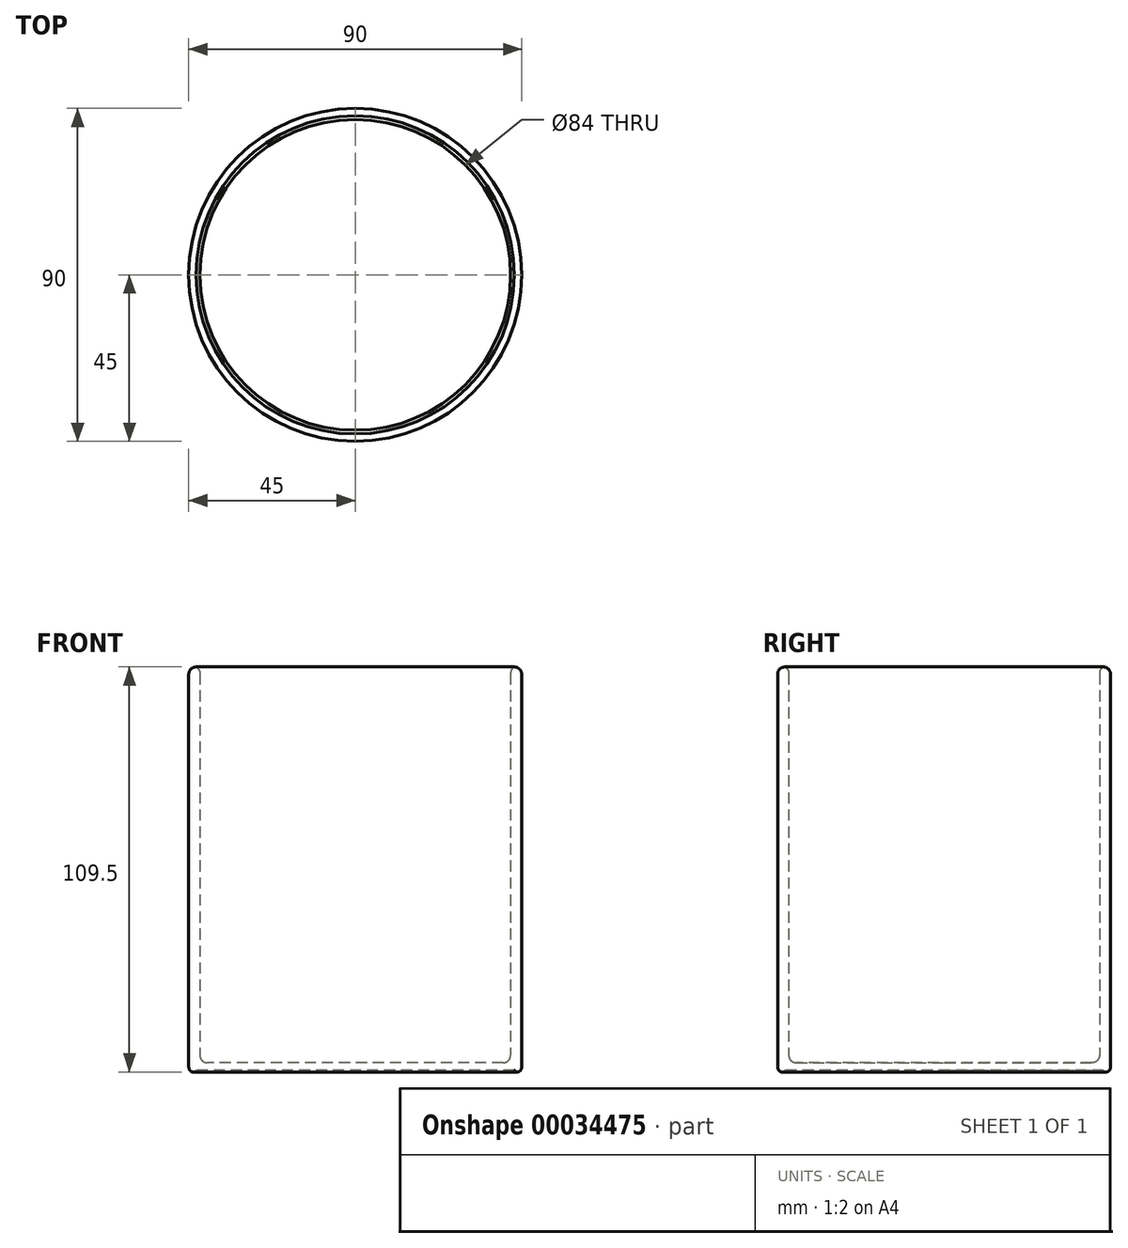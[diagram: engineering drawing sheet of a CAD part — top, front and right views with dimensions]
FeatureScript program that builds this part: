
annotation { "Feature Type Name" : "Feature", "Feature Type Description" : "" }
export const myFeature = defineFeature(function(context is Context, id is Id, definition is map)
    precondition{}
    {
        {
            var Q0;
            Q0=qCreatedBy(makeId("Top.planeOp"),FACE);
            var sketch = newSketch(context, id + "F0", { "sketchPlane" : qUnion([Q0])});
            skCircle(sketch, "E0", {"center": v(0, 0) * mm, "radius": 45 * mm});
            skSolve(sketch);
        }
        {
            var Q0;
            Q0=makeQuery(id+"F0.imprint","IMPRINT",FACE,{"disambiguationData":[TD([[makeQuery(id+"F0.imprint","IMPRINT",EDGE,{"derivedFrom":sQuery(id+"F0.wireOp",EDGE,"E0")}),1.0]])]});
            extrude(context, id + "F1", {"entities" : qUnion([Q0]), "depth" : 110 * mm});
        }
        {
            var Q0;
            Q0=makeQuery(id+"F1.opExtrude","CAP_FACE",FACE,{"disambiguationData":[OSD([sQuery(id+"F0.wireOp",EDGE,"E0")])],"isStart":false});
            shell(context, id + "F2", {"entities" : qUnion([Q0]), "thickness" : 3 * mm});
        }
        {
            var Q0;
            {var subQ0=sQuery(id+"F0.wireOp",EDGE,"E0");Q0=makeQuery(id+"F2.opShell","OFFSET_EDGE",EDGE,{"disambiguationData":[OSD([subQ0]),TDD([makeQuery(id+"F1.opExtrude","CAP_EDGE",EDGE,{"disambiguationData":[OSD([subQ0])],"isStart":true})])]});}
            fillet(context, id + "F3", {"entities" : qUnion([Q0]), "radius" : 2 * mm, "tangentPropagation" : true, "allowEdgeOverflow" : false});
        }
        {
            var Q0;
            Q0=makeQuery(id+"F1.opExtrude","CAP_EDGE",EDGE,{"disambiguationData":[OSD([sQuery(id+"F0.wireOp",EDGE,"E0")])],"isStart":true});
            fillet(context, id + "F4", {"entities" : qUnion([Q0]), "radius" : 2 * mm, "tangentPropagation" : true, "allowEdgeOverflow" : false});
        }
        {
            var Q0;
            Q0=makeQuery(id+"F1.opExtrude","CAP_EDGE",EDGE,{"disambiguationData":[OSD([sQuery(id+"F0.wireOp",EDGE,"E0")])],"isStart":false});
            fillet(context, id + "F5", {"entities" : qUnion([Q0]), "radius" : 2 * mm, "tangentPropagation" : true, "allowEdgeOverflow" : false});
        }
        {
            var Q0;
            {var subQ0=sQuery(id+"F0.wireOp",EDGE,"E0");Q0=makeQuery(id+"F2.opShell","OFFSET_EDGE",EDGE,{"disambiguationData":[OSD([subQ0]),TDD([makeQuery(id+"F1.opExtrude","CAP_EDGE",EDGE,{"disambiguationData":[OSD([subQ0])],"isStart":false})])]});}
            fillet(context, id + "F6", {"entities" : qUnion([Q0]), "radius" : 2 * mm, "tangentPropagation" : true, "allowEdgeOverflow" : false});
        }
        {
            var Q0;
            Q0=makeQuery(id+"F1.opExtrude","CAP_FACE",FACE,{"disambiguationData":[OSD([sQuery(id+"F0.wireOp",EDGE,"E0")])],"isStart":true});
            extrude(context, id + "F7", {"entities" : qUnion([Q0]), "operationType" : NewBodyOperationType.REMOVE, "oppositeDirection" : true, "depth" : 1 * mm});
        }
        {
            var Q0;
            {var subQ0=sQuery(id+"F0.wireOp",EDGE,"E0");Q0=makeQuery(id+"F7.boolean.opBoolean","MERGE",EDGE,{"derivedFrom":[makeQuery(id+"F4.opFillet","BLEND_EDGE",EDGE,{"blendedFrom":[makeQuery(id+"F1.opExtrude","CAP_EDGE",EDGE,{"disambiguationData":[OSD([subQ0])],"isStart":true}),makeQuery(id+"F1.opExtrude","CAP_FACE",FACE,{"disambiguationData":[OSD([subQ0])],"isStart":true})],"blendedInto":[makeQuery(id+"F1.opExtrude","CAP_FACE",FACE,{"disambiguationData":[OSD([subQ0])],"isStart":true})]}),makeQuery(id+"F7.opExtrude","CAP_EDGE",EDGE,{"disambiguationData":[OSD([subQ0])],"isStart":true})]});}
            fillet(context, id + "F8", {"entities" : qUnion([Q0]), "radius" : 1 * mm, "tangentPropagation" : true, "allowEdgeOverflow" : false});
        }
    });
